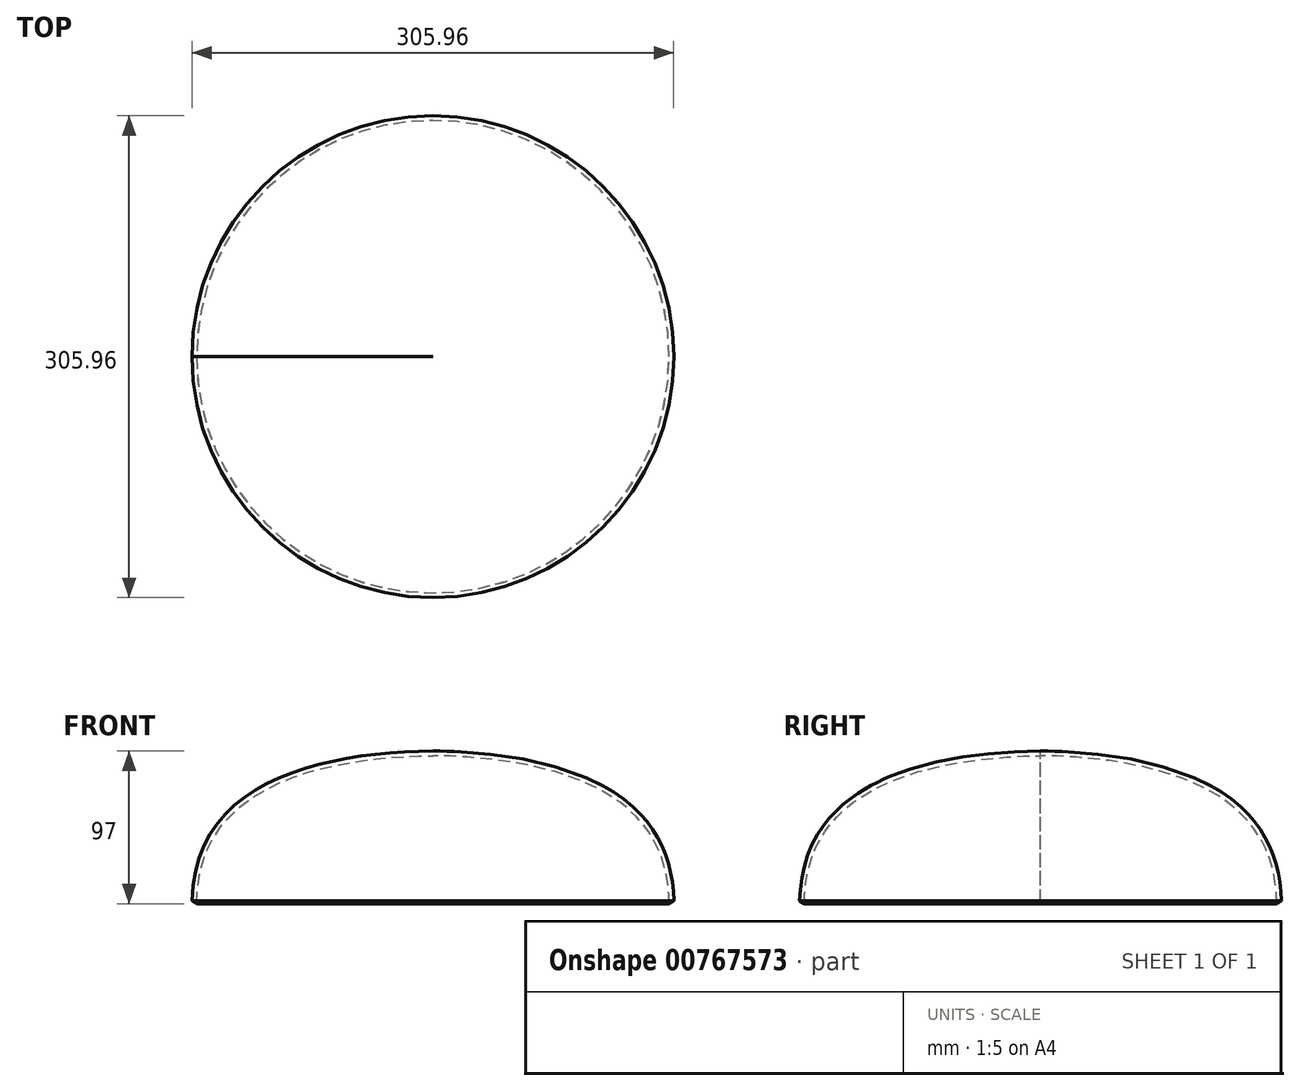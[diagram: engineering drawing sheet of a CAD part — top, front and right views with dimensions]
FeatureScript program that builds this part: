
annotation { "Feature Type Name" : "Feature", "Feature Type Description" : "" }
export const myFeature = defineFeature(function(context is Context, id is Id, definition is map)
    precondition{}
    {
        {
            var Q0;
            Q0=qCreatedBy(makeId("Front.planeOp"),FACE);
            var sketch = newSketch(context, id + "F0", { "sketchPlane" : qUnion([Q0])});
            skLineSegment(sketch, "E0", {"start": v(0, 0) * mm, "end": v(-153, 0) * mm});
            skFitSpline(sketch, "E1", {"points": [v(-153, 0) * mm, v(0, 97) * mm], "startDerivative": vector(0.46, 237.83) * mm, "endDerivative": vector(205.8, 2.76) * mm});
            skLineSegment(sketch, "E2", {"start": v(0, 97) * mm, "end": v(0, 0) * mm});
            skSolve(sketch);
        }
        {
            var Q0;
            Q0=makeQuery(id+"F0.imprint","IMPRINT",FACE,{"disambiguationData":[TD([[makeQuery(id+"F0.imprint","IMPRINT",EDGE,{"derivedFrom":sQuery(id+"F0.wireOp",EDGE,"E0")}),-1.0]])]});
            var Q1;
            Q1=sQuery(id+"F0.wireOp",EDGE,"E2");
            revolve(context, id + "F1", {"surfaceOperationType" : NewSurfaceOperationType.NEW, "entities" : qUnion([Q0]), "axis" : qUnion([Q1]), "revolveType" : RevolveType.FULL});
        }
        {
            var Q0;
            Q0=makeQuery(id+"F1.opRevolve","SWEPT_FACE",FACE,{"disambiguationData":[OSD([sQuery(id+"F0.wireOp",EDGE,"E0")])]});
            shell(context, id + "F2", {"entities" : qUnion([Q0]), "thickness" : 3 * mm});
        }
        {
            var Q0;
            Q0=makeQuery(id+"F1.opRevolve","SWEPT_EDGE",EDGE,{"disambiguationData":[OSD([sQuery(id+"F0.wireOp",EDGE,"E0"),sQuery(id+"F0.wireOp",EDGE,"E1")])]});
            chamfer(context, id + "F3", {"entities" : qUnion([Q0]), "chamferType" : ChamferType.OFFSET_ANGLE, "width" : 1.7 * mm, "oppositeDirection" : false, "angle" : 60 * degree, "tangentPropagation" : true});
        }
    });
